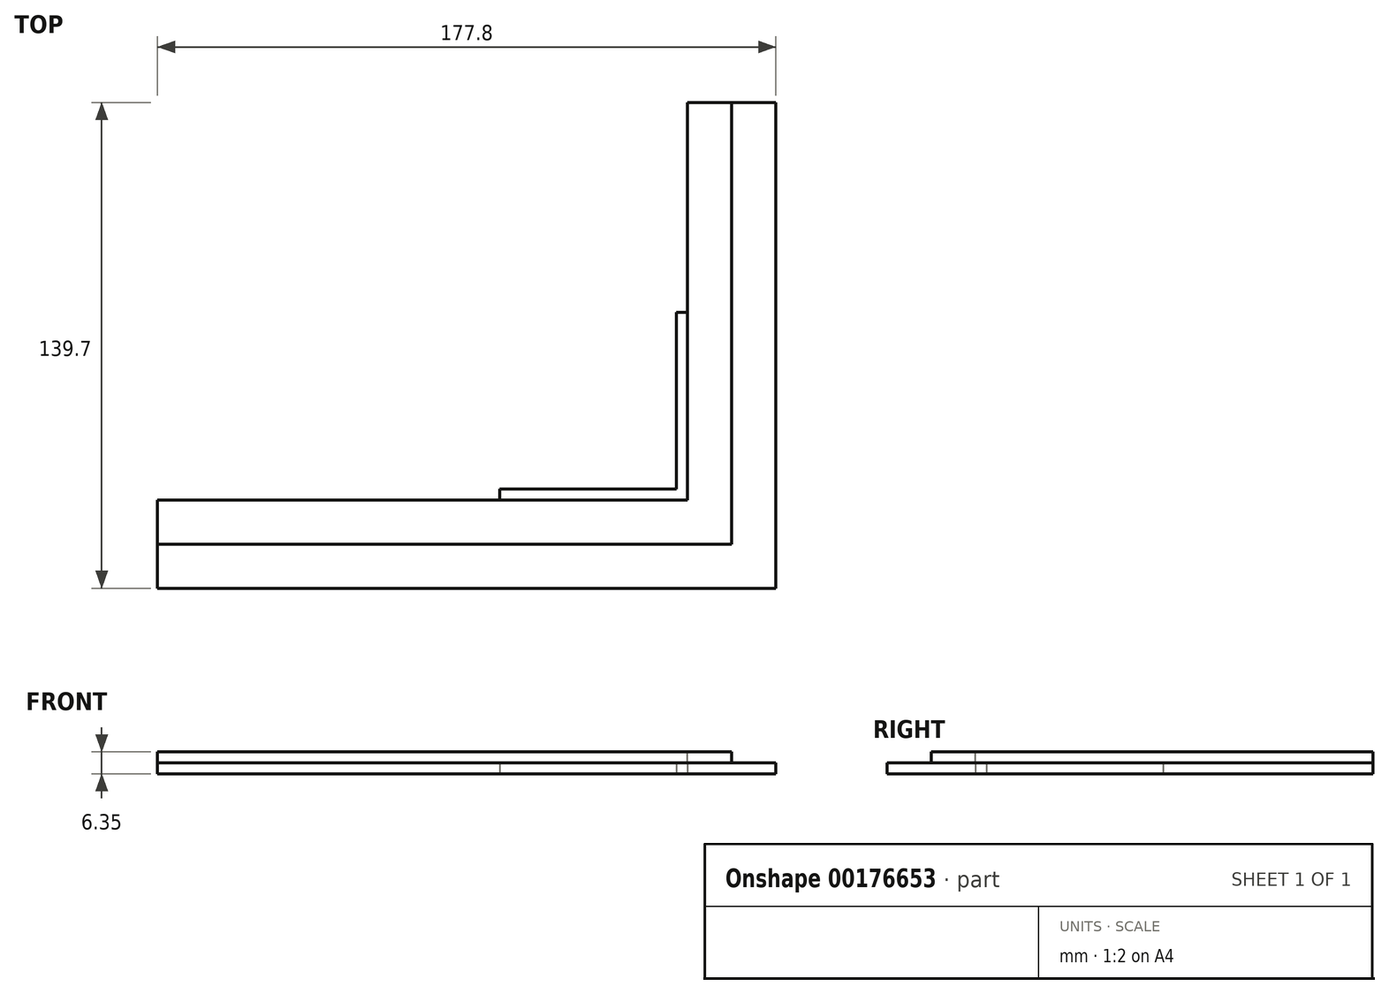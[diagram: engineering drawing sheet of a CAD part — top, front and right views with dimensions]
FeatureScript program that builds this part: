
annotation { "Feature Type Name" : "Feature", "Feature Type Description" : "" }
export const myFeature = defineFeature(function(context is Context, id is Id, definition is map)
    precondition{}
    {
        {
            var Q0;
            Q0=qCreatedBy(makeId("Top.planeOp"),FACE);
            var sketch = newSketch(context, id + "F0", { "sketchPlane" : qUnion([Q0])});
            skLineSegment(sketch, "E0.bottom", {"start": v(0, 0) * mm, "end": v(-177.8, 0) * mm});
            skLineSegment(sketch, "E0.top", {"start": v(0, 139.7) * mm, "end": v(-25.4, 139.7) * mm});
            skLineSegment(sketch, "E0.left", {"start": v(0, 0) * mm, "end": v(0, 139.7) * mm});
            skLineSegment(sketch, "E0.right", {"start": v(-177.8, 0) * mm, "end": v(-177.8, 25.4) * mm});
            skLineSegment(sketch, "E1.top", {"start": v(-25.4, 25.4) * mm, "end": v(-177.8, 25.4) * mm});
            skLineSegment(sketch, "E1.left", {"start": v(-25.4, 139.7) * mm, "end": v(-25.4, 25.4) * mm});
            skLineSegment(sketch, "E2", {"start": v(-25.4, 79.38) * mm, "end": v(-28.58, 79.38) * mm});
            skLineSegment(sketch, "E3", {"start": v(-28.58, 79.38) * mm, "end": v(-28.57, 28.57) * mm});
            skLineSegment(sketch, "E4", {"start": v(-28.57, 28.57) * mm, "end": v(-79.38, 28.57) * mm});
            skLineSegment(sketch, "E5", {"start": v(-79.38, 28.57) * mm, "end": v(-79.38, 25.4) * mm});
            skSolve(sketch);
        }
        {
            var Q0;
            Q0 = qSketchRegion(id + "F0", true);
            extrude(context, id + "F1", {"entities" : qUnion([Q0]), "depth" : 6.35 * mm});
        }
        {
            var Q0;
            Q0=makeQuery(id+"F1.opExtrude","CAP_FACE",FACE,{"disambiguationData":[OSD([sQuery(id+"F0.wireOp",EDGE,"E0.bottom"),sQuery(id+"F0.wireOp",EDGE,"E0.top"),sQuery(id+"F0.wireOp",EDGE,"E0.left"),sQuery(id+"F0.wireOp",EDGE,"E0.right"),sQuery(id+"F0.wireOp",EDGE,"E1.top"),sQuery(id+"F0.wireOp",EDGE,"E1.left")])],"isStart":false});
            var sketch = newSketch(context, id + "F2", { "sketchPlane" : qUnion([Q0])});
            skLineSegment(sketch, "E6.bottom", {"start": v(-12.7, 139.7) * mm, "end": v(0, 139.7) * mm});
            skLineSegment(sketch, "E6.top", {"start": v(-12.7, 0) * mm, "end": v(0, 0) * mm});
            skLineSegment(sketch, "E6.left", {"start": v(-12.7, 139.7) * mm, "end": v(-12.7, 12.7) * mm});
            skLineSegment(sketch, "E6.right", {"start": v(0, 139.7) * mm, "end": v(0, 0) * mm});
            skLineSegment(sketch, "E7.bottom", {"start": v(-177.8, 12.7) * mm, "end": v(-12.7, 12.7) * mm});
            skLineSegment(sketch, "E7.top", {"start": v(-177.8, 0) * mm, "end": v(0, 0) * mm});
            skLineSegment(sketch, "E7.left", {"start": v(-177.8, 12.7) * mm, "end": v(-177.8, 0) * mm});
            skLineSegment(sketch, "E7.right", {"start": v(0, 12.7) * mm, "end": v(0, 0) * mm});
            skSolve(sketch);
        }
        {
            var Q0;
            Q0 = qSketchRegion(id + "F2", true);
            extrude(context, id + "F3", {"entities" : qUnion([Q0]), "operationType" : NewBodyOperationType.REMOVE, "oppositeDirection" : true, "depth" : 3.17 * mm});
        }
        {
            var Q0;
            Q0=makeQuery(id+"F1.opExtrude","CAP_FACE",FACE,{"disambiguationData":[OSD([sQuery(id+"F0.wireOp",EDGE,"E0.bottom"),sQuery(id+"F0.wireOp",EDGE,"E0.top"),sQuery(id+"F0.wireOp",EDGE,"E0.left"),sQuery(id+"F0.wireOp",EDGE,"E0.right"),sQuery(id+"F0.wireOp",EDGE,"E1.top"),sQuery(id+"F0.wireOp",EDGE,"E1.left"),sQuery(id+"F0.wireOp",EDGE,"E2"),sQuery(id+"F0.wireOp",EDGE,"E3"),sQuery(id+"F0.wireOp",EDGE,"E4"),sQuery(id+"F0.wireOp",EDGE,"E5")])],"isStart":false});
            var sketch = newSketch(context, id + "F4", { "sketchPlane" : qUnion([Q0])});
            skLineSegment(sketch, "E8", {"start": v(-79.38, 28.57) * mm, "end": v(-79.38, 25.4) * mm});
            skLineSegment(sketch, "E9", {"start": v(-79.38, 25.4) * mm, "end": v(-25.4, 25.4) * mm});
            skLineSegment(sketch, "E10", {"start": v(-25.4, 79.38) * mm, "end": v(-25.4, 25.4) * mm});
            skLineSegment(sketch, "E11", {"start": v(-25.4, 79.38) * mm, "end": v(-28.58, 79.38) * mm});
            skLineSegment(sketch, "E12", {"start": v(-28.58, 79.38) * mm, "end": v(-28.57, 28.57) * mm});
            skLineSegment(sketch, "E13", {"start": v(-28.57, 28.57) * mm, "end": v(-79.38, 28.57) * mm});
            skSolve(sketch);
        }
        {
            var Q0;
            Q0 = qSketchRegion(id + "F4", true);
            extrude(context, id + "F5", {"entities" : qUnion([Q0]), "operationType" : NewBodyOperationType.REMOVE, "oppositeDirection" : true, "depth" : 3.17 * mm});
        }
    });
